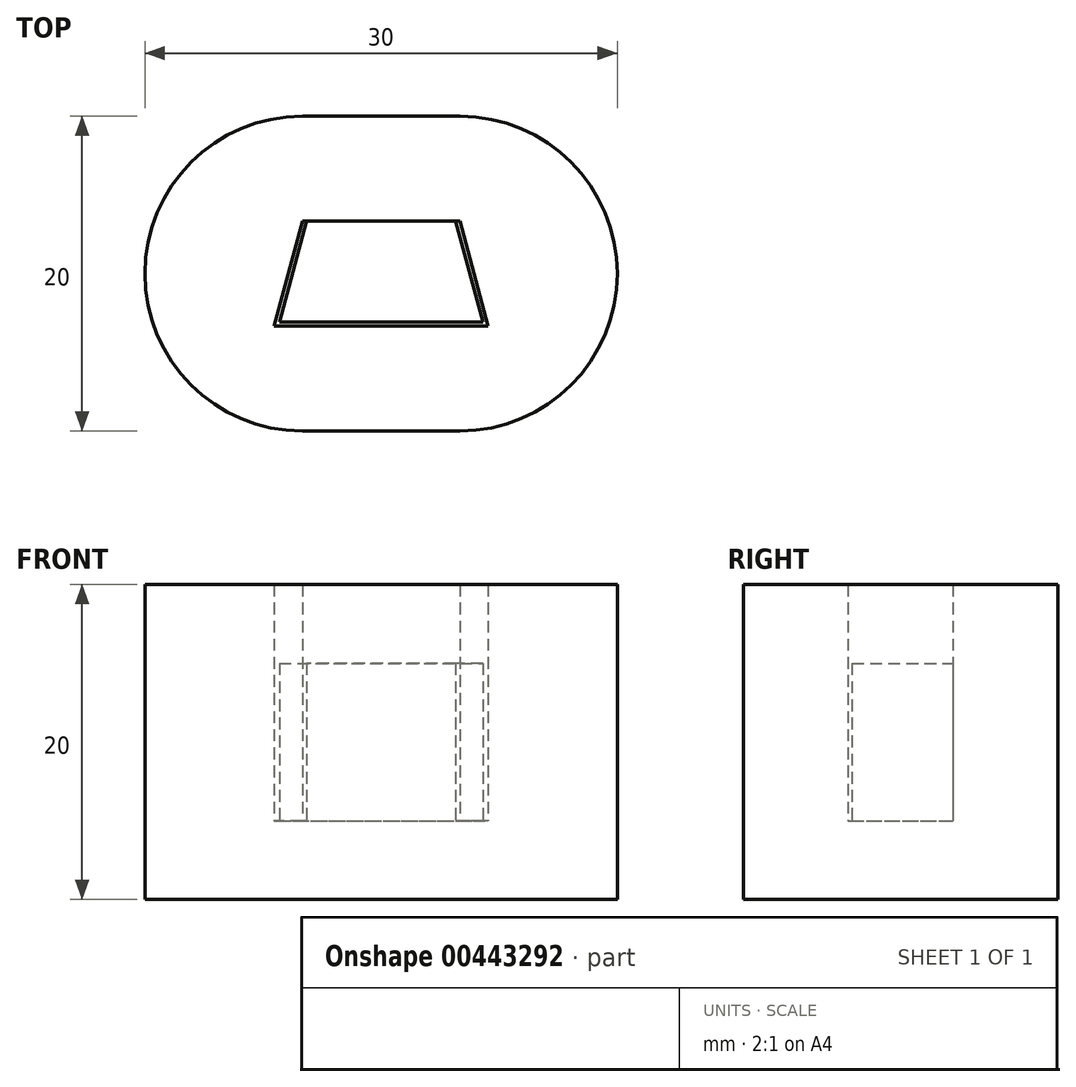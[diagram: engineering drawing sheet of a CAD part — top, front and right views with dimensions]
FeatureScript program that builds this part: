
annotation { "Feature Type Name" : "Feature", "Feature Type Description" : "" }
export const myFeature = defineFeature(function(context is Context, id is Id, definition is map)
    precondition{}
    {
        {
            assignVariable(context, id + "F0", {"name" : "Height", "anyValue" : 20});
        }
        {
            var Q0;
            Q0=qCreatedBy(makeId("Top.planeOp"),FACE);
            var sketch = newSketch(context, id + "F1", { "sketchPlane" : qUnion([Q0])});
            skLineSegment(sketch, "E0.bottom", {"start": v(16.2, 1.57) * mm, "end": v(-13.8, 1.57) * mm});
            skLineSegment(sketch, "E0.top", {"start": v(16.2, -11.76) * mm, "end": v(-13.8, -11.76) * mm});
            skLineSegment(sketch, "E0.left", {"start": v(16.2, 1.57) * mm, "end": v(16.2, -11.76) * mm});
            skLineSegment(sketch, "E0.right", {"start": v(-13.8, 1.57) * mm, "end": v(-13.8, -11.76) * mm});
            skLineSegment(sketch, "E1", {"start": v(-3.8, 1.57) * mm, "end": v(-5.58, -5.1) * mm});
            skLineSegment(sketch, "E2", {"start": v(-5.58, -5.1) * mm, "end": v(1.2, -5.1) * mm});
            skLineSegment(sketch, "E3", {"start": v(1.2, -5.1) * mm, "end": v(8, -5.1) * mm});
            skLineSegment(sketch, "E4", {"start": v(8, -5.1) * mm, "end": v(6.2, 1.57) * mm});
            skLineSegment(sketch, "E5", {"start": v(6.2, 1.57) * mm, "end": v(1.2, 1.57) * mm});
            skLineSegment(sketch, "E6", {"start": v(1.2, 1.57) * mm, "end": v(-3.8, 1.57) * mm});
            skLineSegment(sketch, "E7.bottom", {"start": v(-13.8, 1.57) * mm, "end": v(16.2, 1.57) * mm});
            skLineSegment(sketch, "E7.top", {"start": v(-13.8, 8.24) * mm, "end": v(16.2, 8.24) * mm});
            skLineSegment(sketch, "E7.left", {"start": v(-13.8, 1.57) * mm, "end": v(-13.8, 8.24) * mm});
            skLineSegment(sketch, "E7.right", {"start": v(16.2, 1.57) * mm, "end": v(16.2, 8.24) * mm});
            skLineSegment(sketch, "E8", {"start": v(1.2, 8.24) * mm, "end": v(1.2, 1.57) * mm, "construction": true});
            skLineSegment(sketch, "E9.0", {"start": v(7.67, -4.85) * mm, "end": v(5.98, 1.44) * mm});
            skLineSegment(sketch, "E9.1", {"start": v(-2.04, -4.85) * mm, "end": v(7.67, -4.85) * mm});
            skLineSegment(sketch, "E9.2", {"start": v(-5.25, -4.85) * mm, "end": v(-2.04, -4.85) * mm});
            skLineSegment(sketch, "E9.3", {"start": v(-3.57, 1.44) * mm, "end": v(-5.25, -4.85) * mm});
            skLineSegment(sketch, "E10", {"start": v(-3.57, 1.44) * mm, "end": v(-3.54, 1.57) * mm});
            skLineSegment(sketch, "E11", {"start": v(5.98, 1.44) * mm, "end": v(5.95, 1.57) * mm});
            skSolve(sketch);
        }
        {
            var Q0;
            Q0=makeQuery(id+"F1.imprint","IMPRINT",FACE,{"disambiguationData":[TD([[makeQuery(id+"F1.imprint","IMPRINT",EDGE,{"derivedFrom":sQuery(id+"F1.wireOp",EDGE,"E0.top")}),-1.0]])]});
            extrude(context, id + "F2", {"entities" : qUnion([Q0]), "depth" : (getVariable(context, 'Height')) * mm});
        }
        {
            var Q0;
            Q0=makeQuery(id+"F1.imprint","IMPRINT",FACE,{"disambiguationData":[TD([[makeQuery(id+"F1.imprint","IMPRINT",EDGE,{"derivedFrom":sQuery(id+"F1.wireOp",EDGE,"E7.top")}),-1.0]])]});
            extrude(context, id + "F3", {"entities" : qUnion([Q0]), "depth" : (getVariable(context, 'Height')) * mm});
        }
        {
            var Q0;
            Q0=makeQuery(id+"F1.imprint","IMPRINT",FACE,{"disambiguationData":[TD([[makeQuery(id+"F1.imprint","IMPRINT",EDGE,{"derivedFrom":sQuery(id+"F1.wireOp",EDGE,"E9.0")}),1.0]])]});
            extrude(context, id + "F4", {"entities" : qUnion([Q0]), "operationType" : NewBodyOperationType.ADD, "depth" : (3 * getVariable(context, 'Height') / 4) * mm});
        }
        {
            var Q0;
            Q0=makeQuery(id+"F1.imprint","IMPRINT",FACE,{"disambiguationData":[TD([[makeQuery(id+"F1.imprint","IMPRINT",EDGE,{"derivedFrom":sQuery(id+"F1.wireOp",EDGE,"E9.0")}),1.0]])]});
            var Q1;
            {var subQ3=sQuery(id+"F1.wireOp",EDGE,"E1");Q1=makeQuery(id+"F1.imprint","IMPRINT",FACE,{"disambiguationData":[TD([[makeQuery(id+"F1.imprint","IMPRINT",EDGE,{"derivedFrom":subQ3}),1.0]])]});}
            extrude(context, id + "F5", {"entities" : qUnion([Q0, Q1]), "operationType" : NewBodyOperationType.ADD, "depth" : (getVariable(context, 'Height') / 4) * mm});
        }
        {
            var Q0;
            Q0=makeQuery(id+"F2.opExtrude","SWEPT_EDGE",EDGE,{"disambiguationData":[OSD([sQuery(id+"F1.wireOp",EDGE,"E0.top"),sQuery(id+"F1.wireOp",EDGE,"E0.right")])]});
            var Q1;
            Q1=makeQuery(id+"F2.opExtrude","SWEPT_EDGE",EDGE,{"disambiguationData":[OSD([sQuery(id+"F1.wireOp",EDGE,"E0.top"),sQuery(id+"F1.wireOp",EDGE,"E0.left")])]});
            var Q2;
            Q2=makeQuery(id+"F3.opExtrude","SWEPT_EDGE",EDGE,{"disambiguationData":[OSD([sQuery(id+"F1.wireOp",EDGE,"E7.top"),sQuery(id+"F1.wireOp",EDGE,"E7.left")])]});
            var Q3;
            Q3=makeQuery(id+"F3.opExtrude","SWEPT_EDGE",EDGE,{"disambiguationData":[OSD([sQuery(id+"F1.wireOp",EDGE,"E7.top"),sQuery(id+"F1.wireOp",EDGE,"E7.right")])]});
            fillet(context, id + "F6", {"entities" : qUnion([Q0, Q1, Q2, Q3]), "radius" : 10 * mm, "tangentPropagation" : true, "allowEdgeOverflow" : false});
        }
    });
